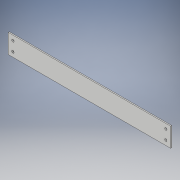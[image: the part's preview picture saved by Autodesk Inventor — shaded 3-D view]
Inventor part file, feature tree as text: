
AUTODESK INVENTOR PART (.ipt)
format: ipt  version: 2017 (Build 210142000, 142)  size: 104,448 bytes
history: native  units: in
note: dims shown in document units (in); Inventor stores cm internally (conversion verified against a paired STEP export)
features: extrude x1, sketch x1
ambient origin geometry x8: Origin, YZ Plane, XZ Plane, XY Plane, X Axis, Y Axis, Z Axis, Center Point
bodies: Solid1 (feature_tree)
feature tree (2):
  extrude  "Extrusion1"  Depth=2.0in
  sketch  "Sketch1"  dims[d0=17.0in d1=2.0in d2=0.5in d3=0.5in d4=1.0in d5=0.25in d6=0.25in d7=0.125in d8=0.0in]
